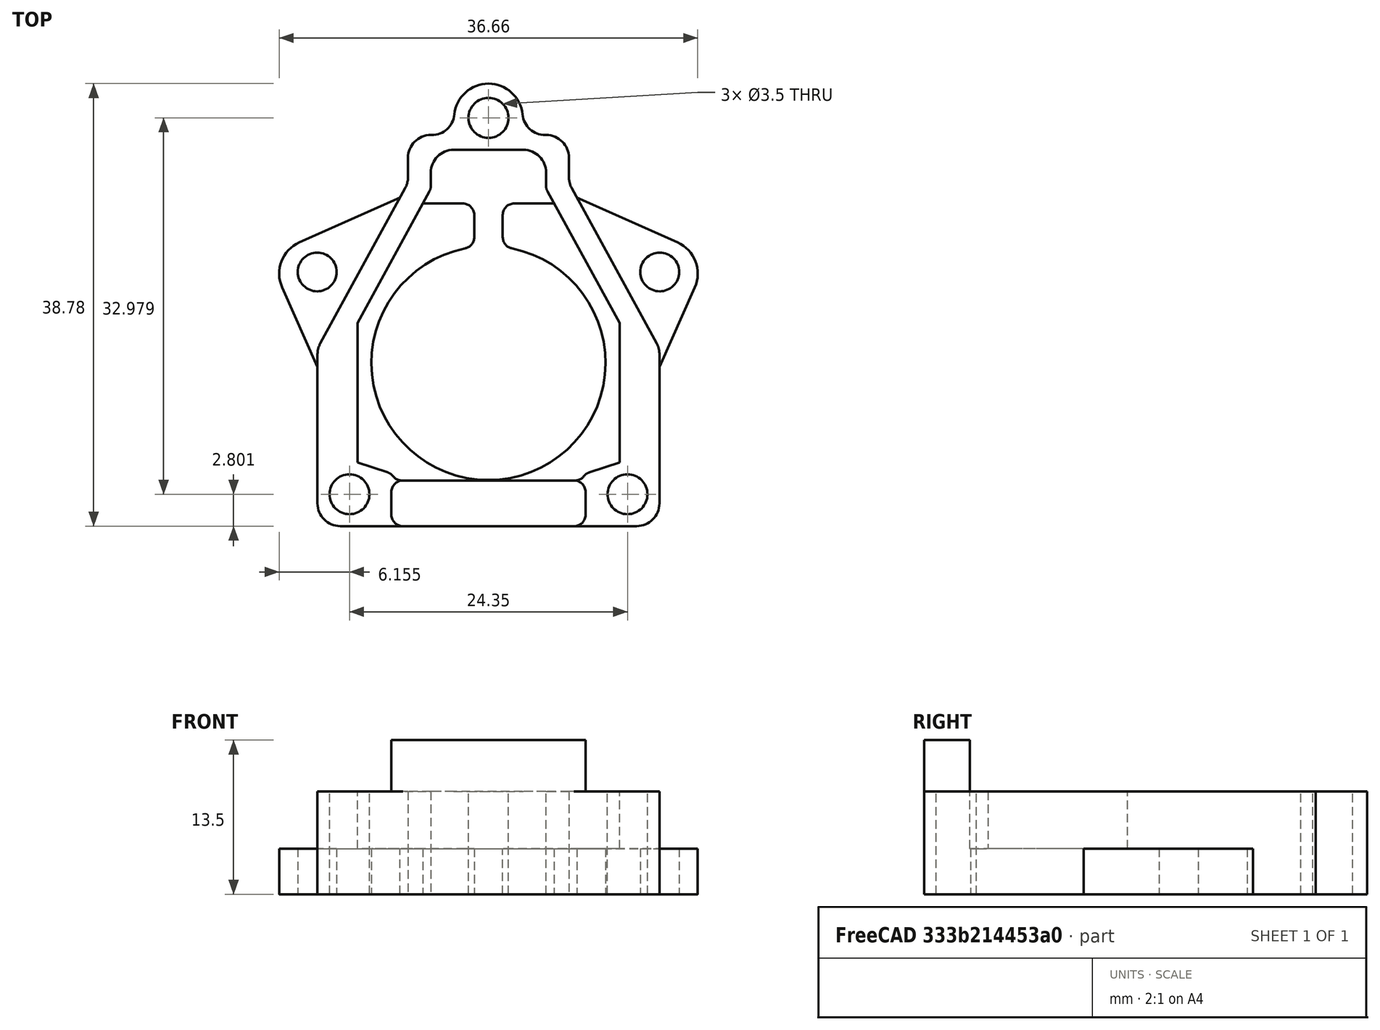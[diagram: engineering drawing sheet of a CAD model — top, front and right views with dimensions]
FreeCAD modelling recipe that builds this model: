
FCSTD DOCUMENT  (FreeCAD 0.14R3692 (Git))
Label: UpperHorizontalMount
License: CC-BY 3.0
LicenseURL: http://creativecommons.org/licenses/by/3.0/
objects: Part::Cut×3, Part::Feature×2, Part::Box×2, Part::Cylinder×2, Part::Fillet×2, Part::Fuse×2, Part::Mirroring×1, App::DocumentObjectGroup×1
note: 14 computed .brp shape members not serialized (recipe doc carries the construction recipe); baked Part::Feature solids carry a one-line shape summary decoded from their .brp

FEATURE [Part::Feature] Part__Feature  label="UpperVerticalMount"
  shape: bbox 29.95 x 38.78 x 13.5 mm, 60 faces (baked)
FEATURE [Part::Box] Box  label="Cube"
  Height = 4
  Length = 14
  Placement = pos=(-14,5.5,5.3) rot=(0,0,1;0.418879rad)
  Width = 13
FEATURE [Part::Cylinder] Cylinder
  Angle = 360
  Height = 17
  Placement = pos=(-15,16,0) rot=(0,0,1;0rad)
  Radius = 1.7
FEATURE [Part::Box] Box001  label="Cube001"
  Height = 13
  Length = 23
  Placement = pos=(-5,-2.5,-0.7) rot=(0,0,1;1.0821rad)
  Width = 13
FEATURE [Part::Cut] Cut
  Base = -> Box
  Tool = -> Box001
FEATURE [Part::Fillet] Fillet
  Base = -> Cut
  Edges = 1 edges r=3: [Edge2]
FEATURE [Part::Cut] Cut001
  Base = -> Fillet
  Tool = -> Cylinder
FEATURE [Part::Mirroring] Part__Mirroring  label="Cut001 (Mirror #1)"
  Base = (0,0,0)
  Normal = (1,0,0)
  Source = -> Cut001
FEATURE [Part::Fillet] Fillet001
  Base = -> Cut
  Edges = 1 edges r=3: [Edge2]
FEATURE [Part::Cylinder] Cylinder002
  Angle = 360
  Height = 17
  Placement = pos=(-15,16,0) rot=(0,0,1;0rad)
  Radius = 1.7
FEATURE [Part::Cut] Cut002
  Base = -> Fillet001
  Tool = -> Cylinder002
FEATURE [Part::Fuse] Fusion
  Base = -> Part__Feature
  Tool = -> Part__Mirroring
FEATURE [Part::Fuse] Fusion001  label="UpperHorizontalMount"
  Base = -> Cut002
  Placement = pos=(0,0,8) rot=(0,1,0;3.14159rad)
  Tool = -> Fusion
FEATURE [App::DocumentObjectGroup] Group  label="Working"
  Group = -> [Cut]
FEATURE [Part::Feature] Shape  label="section"
  shape: bbox 36.65 x 38.78 x 2e-07 mm, 0 faces, 0 solids (baked)
